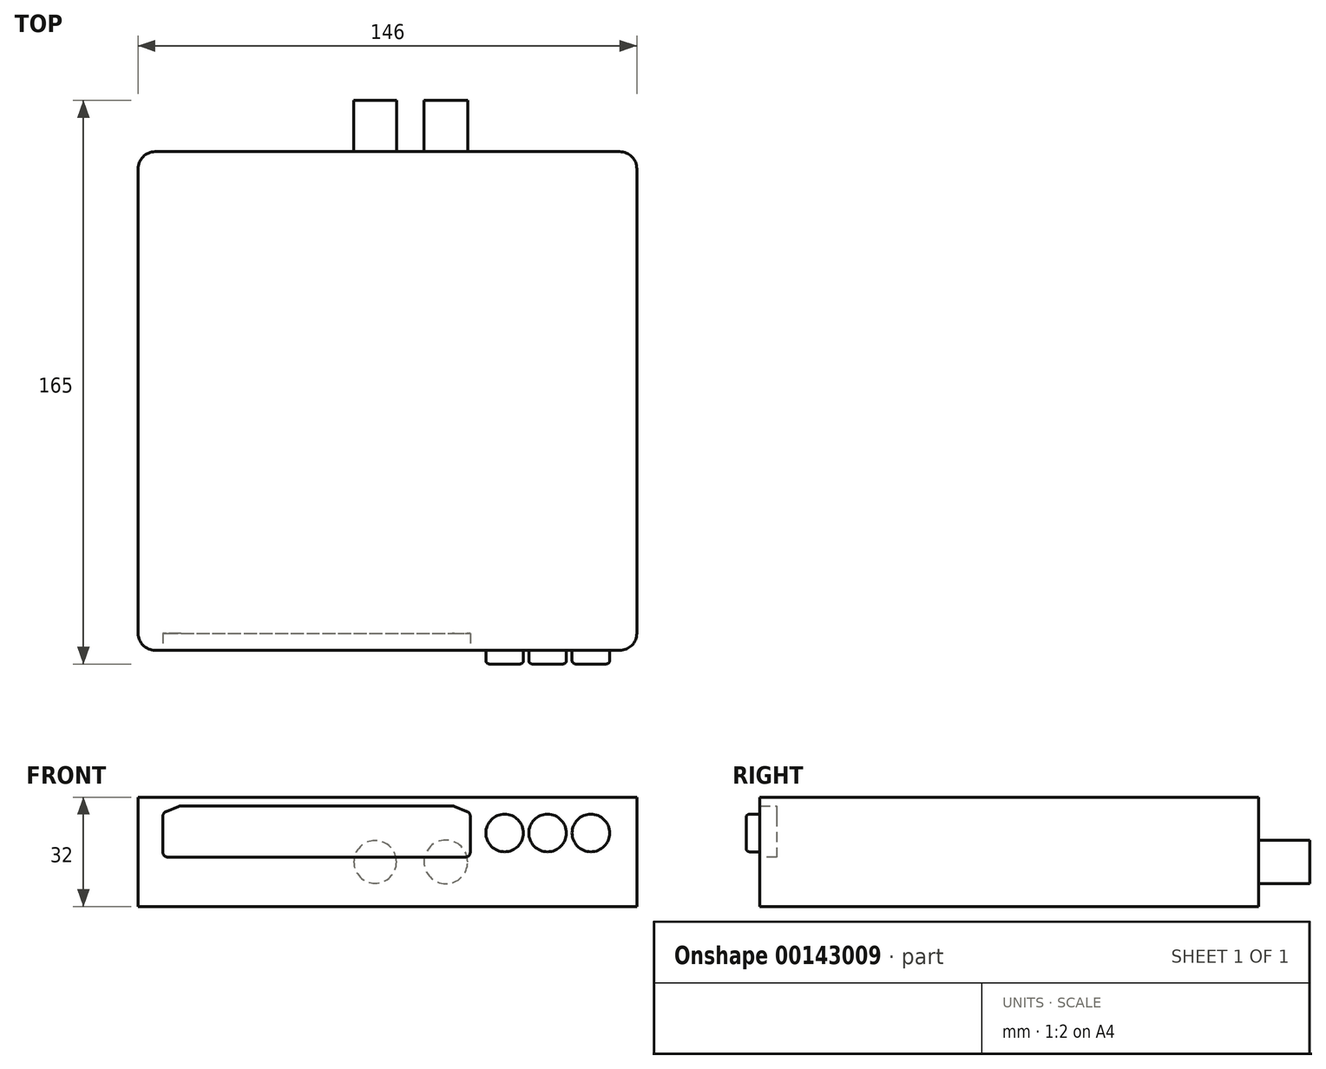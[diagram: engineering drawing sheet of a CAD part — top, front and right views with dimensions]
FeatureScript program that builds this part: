
annotation { "Feature Type Name" : "Feature", "Feature Type Description" : "" }
export const myFeature = defineFeature(function(context is Context, id is Id, definition is map)
    precondition{}
    {
        {
            var Q0;
            Q0=qCreatedBy(makeId("Top.planeOp"),FACE);
            var sketch = newSketch(context, id + "F0", { "sketchPlane" : qUnion([Q0])});
            skLineSegment(sketch, "E0.bottom", {"start": v(5, 0) * mm, "end": v(141, 0) * mm});
            skLineSegment(sketch, "E0.top", {"start": v(5, 146) * mm, "end": v(141, 146) * mm});
            skLineSegment(sketch, "E0.left", {"start": v(0, 5) * mm, "end": v(0, 141) * mm});
            skLineSegment(sketch, "E0.right", {"start": v(146, 5) * mm, "end": v(146, 141) * mm});
            skPoint(sketch, "E1.visualSharp", {"position": v(0, 146) * mm});
            skArc(sketch, "E1.filletArc", {"start": v(5, 146) * mm, "mid": v(1.46, 144.54) * mm, "end": v(0, 141) * mm});
            skPoint(sketch, "E2.visualSharp", {"position": v(146, 0) * mm});
            skArc(sketch, "E2.filletArc", {"start": v(141, 0) * mm, "mid": v(144.54, 1.46) * mm, "end": v(146, 5) * mm});
            skPoint(sketch, "E3.visualSharp", {"position": v(0, 0) * mm});
            skArc(sketch, "E3.filletArc", {"start": v(0, 5) * mm, "mid": v(1.46, 1.46) * mm, "end": v(5, 0) * mm});
            skPoint(sketch, "E4.visualSharp", {"position": v(146, 146) * mm});
            skArc(sketch, "E4.filletArc", {"start": v(146, 141) * mm, "mid": v(144.54, 144.54) * mm, "end": v(141, 146) * mm});
            skSolve(sketch);
        }
        {
            var Q0;
            Q0 = qSketchRegion(id + "F0", true);
            extrude(context, id + "F1", {"entities" : qUnion([Q0]), "depth" : 32 * mm});
        }
        {
            var Q0;
            Q0=makeQuery(id+"F1.opExtrude","SWEPT_FACE",FACE,{"disambiguationData":[OSD([sQuery(id+"F0.wireOp",EDGE,"E0.bottom")])]});
            var sketch = newSketch(context, id + "F2", { "sketchPlane" : qUnion([Q0])});
            skLineSegment(sketch, "E5.bottom", {"start": v(7.25, 29.43) * mm, "end": v(97.25, 29.43) * mm});
            skLineSegment(sketch, "E5.top", {"start": v(7.25, 14.43) * mm, "end": v(97.25, 14.43) * mm});
            skLineSegment(sketch, "E5.left", {"start": v(7.25, 29.43) * mm, "end": v(7.25, 14.43) * mm});
            skLineSegment(sketch, "E5.right", {"start": v(97.25, 29.43) * mm, "end": v(97.25, 14.43) * mm});
            skLineSegment(sketch, "E6", {"start": v(132.44, 21.5) * mm, "end": v(107.3, 21.5) * mm, "construction": true});
            skPoint(sketch, "E7", {"position": v(119.87, 21.5) * mm});
            skCircle(sketch, "E8", {"center": v(107.3, 21.5) * mm, "radius": 5.5 * mm});
            skCircle(sketch, "E9", {"center": v(119.87, 21.5) * mm, "radius": 5.5 * mm});
            skCircle(sketch, "E10", {"center": v(132.55, 21.5) * mm, "radius": 5.5 * mm});
            skSolve(sketch);
        }
        {
            var Q0;
            Q0=makeQuery(id+"F2.imprint","IMPRINT",FACE,{"disambiguationData":[TD([[makeQuery(id+"F2.imprint","IMPRINT",EDGE,{"derivedFrom":sQuery(id+"F2.wireOp",EDGE,"E8")}),1.0]])]});
            var Q1;
            Q1=makeQuery(id+"F2.imprint","IMPRINT",FACE,{"disambiguationData":[TD([[makeQuery(id+"F2.imprint","IMPRINT",EDGE,{"derivedFrom":sQuery(id+"F2.wireOp",EDGE,"E9")}),1.0]])]});
            var Q2;
            Q2=makeQuery(id+"F2.imprint","IMPRINT",FACE,{"disambiguationData":[TD([[makeQuery(id+"F2.imprint","IMPRINT",EDGE,{"derivedFrom":sQuery(id+"F2.wireOp",EDGE,"E10")}),1.0]])]});
            extrude(context, id + "F3", {"entities" : qUnion([Q0, Q1, Q2]), "operationType" : NewBodyOperationType.ADD, "depth" : 4 * mm});
        }
        {
            var Q0;
            Q0=makeQuery(id+"F3.opExtrude","CAP_FACE",FACE,{"disambiguationData":[OSD([sQuery(id+"F2.wireOp",EDGE,"E8")])],"isStart":false});
            var Q1;
            Q1=makeQuery(id+"F3.opExtrude","CAP_FACE",FACE,{"disambiguationData":[OSD([sQuery(id+"F2.wireOp",EDGE,"E9")])],"isStart":false});
            var Q2;
            Q2=makeQuery(id+"F3.opExtrude","CAP_FACE",FACE,{"disambiguationData":[OSD([sQuery(id+"F2.wireOp",EDGE,"E10")])],"isStart":false});
            fillet(context, id + "F4", {"entities" : qUnion([Q0, Q1, Q2]), "radius" : 1 * mm, "tangentPropagation" : true, "allowEdgeOverflow" : false});
        }
        {
            var Q0;
            Q0=makeQuery(id+"F2.imprint","IMPRINT",FACE,{"disambiguationData":[TD([[makeQuery(id+"F2.imprint","IMPRINT",EDGE,{"derivedFrom":sQuery(id+"F2.wireOp",EDGE,"E5.bottom")}),-1.0]])]});
            extrude(context, id + "F5", {"entities" : qUnion([Q0]), "operationType" : NewBodyOperationType.REMOVE, "oppositeDirection" : true, "depth" : 5 * mm});
        }
        {
            var Q0;
            Q0=makeQuery(id+"F5.boolean.opBoolean","COPY",EDGE,{"derivedFrom":makeQuery(id+"F5.opExtrude","SWEPT_EDGE",EDGE,{"disambiguationData":[OSD([sQuery(id+"F2.wireOp",EDGE,"E5.bottom"),sQuery(id+"F2.wireOp",EDGE,"E5.left")])]})});
            chamfer(context, id + "F6", {"entities" : qUnion([Q0]), "chamferType" : ChamferType.TWO_OFFSETS, "width1" : 2 * mm, "oppositeDirection" : false, "width2" : 5 * mm, "tangentPropagation" : true});
        }
        {
            var Q0;
            Q0=makeQuery(id+"F5.boolean.opBoolean","COPY",EDGE,{"derivedFrom":makeQuery(id+"F5.opExtrude","SWEPT_EDGE",EDGE,{"disambiguationData":[OSD([sQuery(id+"F2.wireOp",EDGE,"E5.bottom"),sQuery(id+"F2.wireOp",EDGE,"E5.right")])]})});
            chamfer(context, id + "F7", {"entities" : qUnion([Q0]), "chamferType" : ChamferType.TWO_OFFSETS, "width1" : 5 * mm, "oppositeDirection" : false, "width2" : 2 * mm, "tangentPropagation" : true});
        }
        {
            var Q0;
            {var subQ0=sQuery(id+"F2.wireOp",EDGE,"E5.bottom");Q0=makeQuery(id+"F7.opChamfer","BLEND_EDGE",EDGE,{"blendedFrom":[makeQuery(id+"F5.boolean.opBoolean","COPY",EDGE,{"derivedFrom":makeQuery(id+"F5.opExtrude","SWEPT_EDGE",EDGE,{"disambiguationData":[OSD([subQ0,sQuery(id+"F2.wireOp",EDGE,"E5.right")])]})}),makeQuery(id+"F5.boolean.opBoolean","COPY",FACE,{"derivedFrom":makeQuery(id+"F5.opExtrude","SWEPT_FACE",FACE,{"disambiguationData":[OSD([subQ0])]})})],"blendedInto":[makeQuery(id+"F5.boolean.opBoolean","COPY",FACE,{"derivedFrom":makeQuery(id+"F5.opExtrude","SWEPT_FACE",FACE,{"disambiguationData":[OSD([subQ0])]})})]});}
            var Q1;
            {var subQ0=sQuery(id+"F2.wireOp",EDGE,"E5.right");Q1=makeQuery(id+"F7.opChamfer","BLEND_EDGE",EDGE,{"blendedFrom":[makeQuery(id+"F5.boolean.opBoolean","COPY",EDGE,{"derivedFrom":makeQuery(id+"F5.opExtrude","SWEPT_EDGE",EDGE,{"disambiguationData":[OSD([sQuery(id+"F2.wireOp",EDGE,"E5.bottom"),subQ0])]})}),makeQuery(id+"F5.boolean.opBoolean","COPY",FACE,{"derivedFrom":makeQuery(id+"F5.opExtrude","SWEPT_FACE",FACE,{"disambiguationData":[OSD([subQ0])]})})],"blendedInto":[makeQuery(id+"F5.boolean.opBoolean","COPY",FACE,{"derivedFrom":makeQuery(id+"F5.opExtrude","SWEPT_FACE",FACE,{"disambiguationData":[OSD([subQ0])]})})]});}
            var Q2;
            Q2=makeQuery(id+"F5.boolean.opBoolean","COPY",EDGE,{"derivedFrom":makeQuery(id+"F5.opExtrude","SWEPT_EDGE",EDGE,{"disambiguationData":[OSD([sQuery(id+"F2.wireOp",EDGE,"E5.top"),sQuery(id+"F2.wireOp",EDGE,"E5.right")])]})});
            var Q3;
            Q3=makeQuery(id+"F5.boolean.opBoolean","COPY",EDGE,{"derivedFrom":makeQuery(id+"F5.opExtrude","SWEPT_EDGE",EDGE,{"disambiguationData":[OSD([sQuery(id+"F2.wireOp",EDGE,"E5.top"),sQuery(id+"F2.wireOp",EDGE,"E5.left")])]})});
            var Q4;
            {var subQ0=sQuery(id+"F2.wireOp",EDGE,"E5.left");Q4=makeQuery(id+"F6.opChamfer","BLEND_EDGE",EDGE,{"blendedFrom":[makeQuery(id+"F5.boolean.opBoolean","COPY",EDGE,{"derivedFrom":makeQuery(id+"F5.opExtrude","SWEPT_EDGE",EDGE,{"disambiguationData":[OSD([sQuery(id+"F2.wireOp",EDGE,"E5.bottom"),subQ0])]})}),makeQuery(id+"F5.boolean.opBoolean","COPY",FACE,{"derivedFrom":makeQuery(id+"F5.opExtrude","SWEPT_FACE",FACE,{"disambiguationData":[OSD([subQ0])]})})],"blendedInto":[makeQuery(id+"F5.boolean.opBoolean","COPY",FACE,{"derivedFrom":makeQuery(id+"F5.opExtrude","SWEPT_FACE",FACE,{"disambiguationData":[OSD([subQ0])]})})]});}
            var Q5;
            {var subQ0=sQuery(id+"F2.wireOp",EDGE,"E5.bottom");Q5=makeQuery(id+"F6.opChamfer","BLEND_EDGE",EDGE,{"blendedFrom":[makeQuery(id+"F5.boolean.opBoolean","COPY",EDGE,{"derivedFrom":makeQuery(id+"F5.opExtrude","SWEPT_EDGE",EDGE,{"disambiguationData":[OSD([subQ0,sQuery(id+"F2.wireOp",EDGE,"E5.left")])]})}),makeQuery(id+"F5.boolean.opBoolean","COPY",FACE,{"derivedFrom":makeQuery(id+"F5.opExtrude","SWEPT_FACE",FACE,{"disambiguationData":[OSD([subQ0])]})})],"blendedInto":[makeQuery(id+"F5.boolean.opBoolean","COPY",FACE,{"derivedFrom":makeQuery(id+"F5.opExtrude","SWEPT_FACE",FACE,{"disambiguationData":[OSD([subQ0])]})})]});}
            fillet(context, id + "F8", {"entities" : qUnion([Q0, Q1, Q2, Q3, Q4, Q5]), "radius" : 1.5 * mm, "tangentPropagation" : true, "allowEdgeOverflow" : false});
        }
        {
            var Q0;
            Q0=makeQuery(id+"F1.opExtrude","SWEPT_FACE",FACE,{"disambiguationData":[OSD([sQuery(id+"F0.wireOp",EDGE,"E0.top")])]});
            var sketch = newSketch(context, id + "F9", { "sketchPlane" : qUnion([Q0])});
            skLineSegment(sketch, "E11", {"start": v(-90.09, 13.04) * mm, "end": v(-69.4, 13.04) * mm, "construction": true});
            skCircle(sketch, "E12", {"center": v(-90.09, 13.04) * mm, "radius": 6.4 * mm});
            skCircle(sketch, "E13", {"center": v(-69.4, 13.04) * mm, "radius": 6.24 * mm});
            skSolve(sketch);
        }
        {
            var Q0;
            Q0 = qSketchRegion(id + "F9", true);
            extrude(context, id + "F10", {"entities" : qUnion([Q0]), "operationType" : NewBodyOperationType.ADD, "depth" : 15 * mm});
        }
    });
